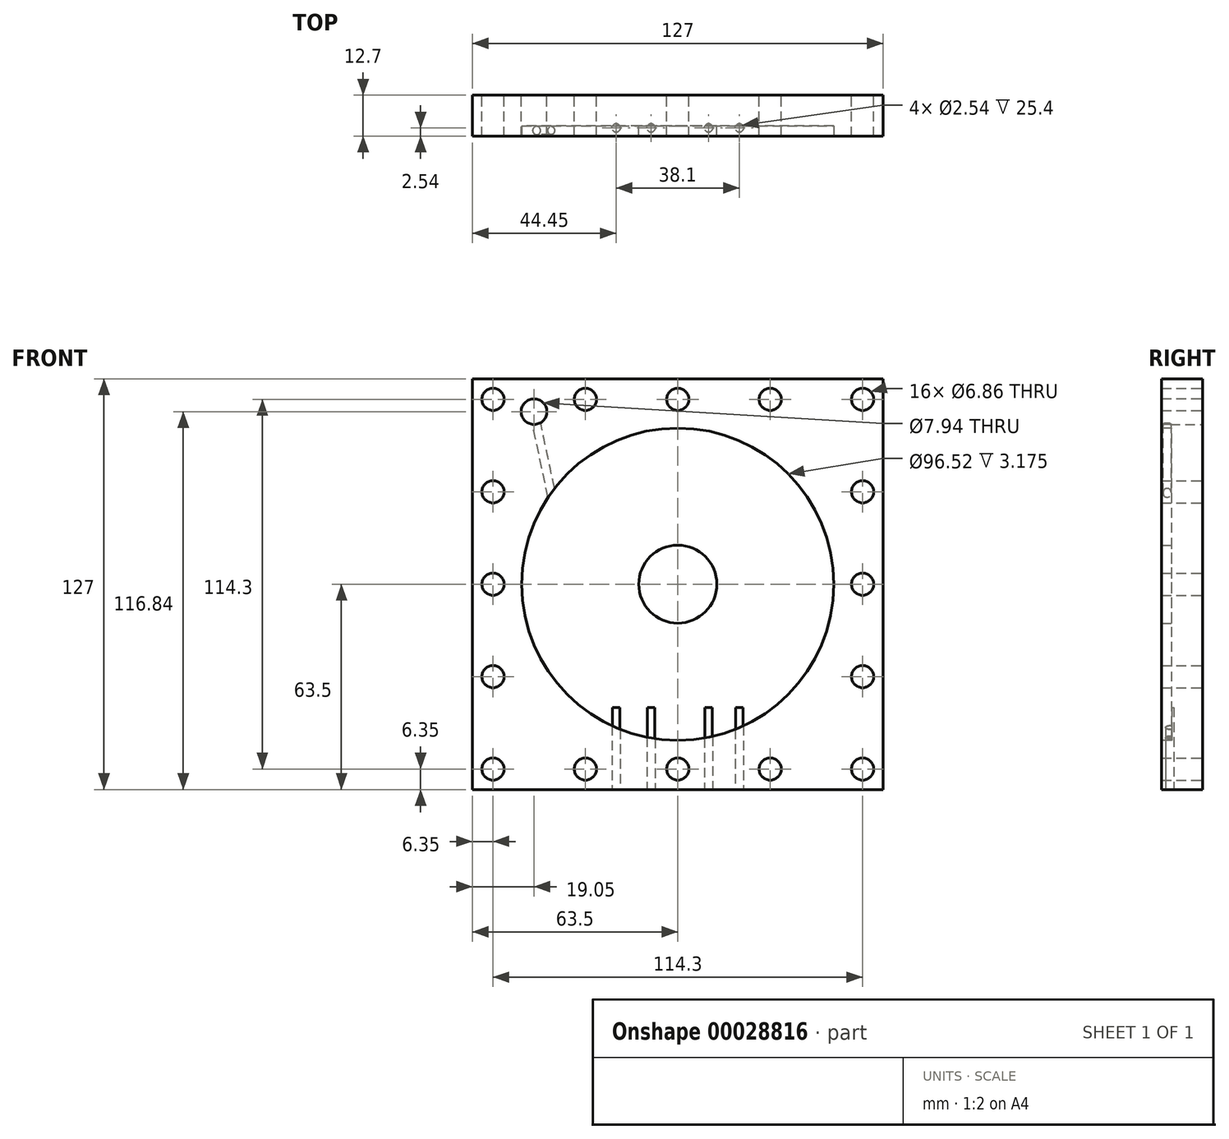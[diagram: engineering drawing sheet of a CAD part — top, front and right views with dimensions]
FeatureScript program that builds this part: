
annotation { "Feature Type Name" : "Feature", "Feature Type Description" : "" }
export const myFeature = defineFeature(function(context is Context, id is Id, definition is map)
    precondition{}
    {
        {
            var Q0;
            Q0=qCreatedBy(makeId("Front.planeOp"),FACE);
            var sketch = newSketch(context, id + "F0", { "sketchPlane" : qUnion([Q0])});
            skLineSegment(sketch, "E0.rect.bottom", {"start": v(63.5, 63.5) * mm, "end": v(-63.5, 63.5) * mm});
            skLineSegment(sketch, "E0.rect.top", {"start": v(63.5, -63.5) * mm, "end": v(-63.5, -63.5) * mm});
            skLineSegment(sketch, "E0.rect.left", {"start": v(63.5, 63.5) * mm, "end": v(63.5, -63.5) * mm});
            skLineSegment(sketch, "E0.rect.right", {"start": v(-63.5, 63.5) * mm, "end": v(-63.5, -63.5) * mm});
            skPoint(sketch, "E0.rect.middle", {"position": v(0, 0) * mm});
            skCircle(sketch, "E1", {"center": v(-44.45, 53.34) * mm, "radius": 3.97 * mm});
            skCircle(sketch, "E2", {"center": v(0, 0) * mm, "radius": 47.56 * mm, "construction": true});
            skLineSegment(sketch, "E3.rect.bottom", {"start": v(-57.15, 57.15) * mm, "end": v(57.15, 57.15) * mm, "construction": true});
            skLineSegment(sketch, "E3.rect.top", {"start": v(-57.15, -57.15) * mm, "end": v(57.15, -57.15) * mm, "construction": true});
            skLineSegment(sketch, "E3.rect.left", {"start": v(-57.15, 57.15) * mm, "end": v(-57.15, -57.15) * mm, "construction": true});
            skLineSegment(sketch, "E3.rect.right", {"start": v(57.15, 57.15) * mm, "end": v(57.15, -57.15) * mm, "construction": true});
            skPoint(sketch, "E4", {"position": v(0, 57.15) * mm});
            skPoint(sketch, "E5", {"position": v(57.15, 0) * mm});
            skPoint(sketch, "E6", {"position": v(0, -57.15) * mm});
            skPoint(sketch, "E7", {"position": v(-57.15, 0) * mm});
            skCircle(sketch, "E8", {"center": v(-57.15, 57.15) * mm, "radius": 3.43 * mm});
            skCircle(sketch, "E9", {"center": v(0, 57.15) * mm, "radius": 3.43 * mm});
            skCircle(sketch, "E10", {"center": v(57.15, 57.15) * mm, "radius": 3.43 * mm});
            skCircle(sketch, "E11", {"center": v(57.15, 0) * mm, "radius": 3.43 * mm});
            skCircle(sketch, "E12", {"center": v(57.15, -57.15) * mm, "radius": 3.43 * mm});
            skCircle(sketch, "E13", {"center": v(0, -57.15) * mm, "radius": 3.43 * mm});
            skCircle(sketch, "E14", {"center": v(-57.15, -57.15) * mm, "radius": 3.43 * mm});
            skCircle(sketch, "E15", {"center": v(-57.15, 0) * mm, "radius": 3.43 * mm});
            skLineSegment(sketch, "E16.rect.bottom", {"start": v(-50, 50) * mm, "end": v(50, 50) * mm, "construction": true});
            skLineSegment(sketch, "E16.rect.top", {"start": v(-50, -50) * mm, "end": v(50, -50) * mm, "construction": true});
            skLineSegment(sketch, "E16.rect.left", {"start": v(-50, 50) * mm, "end": v(-50, -50) * mm, "construction": true});
            skLineSegment(sketch, "E16.rect.right", {"start": v(50, 50) * mm, "end": v(50, -50) * mm, "construction": true});
            skCircle(sketch, "E17", {"center": v(28.57, 57.15) * mm, "radius": 3.43 * mm});
            skCircle(sketch, "E18", {"center": v(57.15, 28.58) * mm, "radius": 3.43 * mm});
            skCircle(sketch, "E19", {"center": v(57.15, -28.58) * mm, "radius": 3.43 * mm});
            skCircle(sketch, "E20", {"center": v(28.58, -57.15) * mm, "radius": 3.43 * mm});
            skCircle(sketch, "E21", {"center": v(-28.58, -57.15) * mm, "radius": 3.43 * mm});
            skCircle(sketch, "E22", {"center": v(-57.15, -28.58) * mm, "radius": 3.43 * mm});
            skCircle(sketch, "E23", {"center": v(-57.15, 28.58) * mm, "radius": 3.43 * mm});
            skCircle(sketch, "E24", {"center": v(-28.58, 57.15) * mm, "radius": 3.43 * mm});
            skSolve(sketch);
        }
        {
            var Q0;
            Q0=qSketchRegion(id+"F0",true);
            var Q1;
            {var subQ21=sQuery(id+"F0.wireOp",EDGE,"f6949425-b88c-4a0e-8302-07c829dae053.0");var subQ27=sQuery(id+"F0.wireOp",EDGE,"5bd9be1d-ee3e-4944-9718-c5885c81100e");var subQ29=makeQuery(id+"F0.imprint","INTERSECT",VERTEX,{"derivedFrom":[subQ21,subQ27]});Q1=makeQuery(id+"F0.imprint","IMPRINT",FACE,{"disambiguationData":[TD([[makeQuery(id+"F0.imprint","IMPRINT",EDGE,{"disambiguationData":[TD([[subQ29,-1.0]])],"derivedFrom":subQ21}),-1.0]])]});}
            extrude(context, id + "F1", {"entities" : qUnion([Q0, Q1]), "depth" : 12.7 * mm});
        }
        {
            var Q0;
            Q0=makeQuery(id+"F1.opExtrude","CAP_FACE",FACE,{"disambiguationData":[OSD([sQuery(id+"F0.wireOp",EDGE,"E0.rect.bottom"),sQuery(id+"F0.wireOp",EDGE,"E0.rect.top"),sQuery(id+"F0.wireOp",EDGE,"E0.rect.left"),sQuery(id+"F0.wireOp",EDGE,"E0.rect.right"),sQuery(id+"F0.wireOp",EDGE,"1b772a9f-1761-4584-9b2b-9508be88e127"),sQuery(id+"F0.wireOp",EDGE,"5bd9be1d-ee3e-4944-9718-c5885c81100e"),sQuery(id+"F0.wireOp",EDGE,"a4b3396b-acb1-4126-9ecc-f22d3d9e1673"),sQuery(id+"F0.wireOp",EDGE,"6f9071d3-dfce-459a-96f3-6cfad81b1998"),sQuery(id+"F0.wireOp",EDGE,"8e253895-448c-4740-8d73-7ad6095a0958"),sQuery(id+"F0.wireOp",EDGE,"49ddc21f-956a-45ed-accb-e36c5fb570fd"),sQuery(id+"F0.wireOp",EDGE,"4c855955-bd80-4a33-8133-648448e085db"),sQuery(id+"F0.wireOp",EDGE,"5388e59b-5754-40e4-abb9-c8fe2573278b"),sQuery(id+"F0.wireOp",EDGE,"cb97a597-6742-4d9a-a243-e93a22987a54"),sQuery(id+"F0.wireOp",EDGE,"2f3ac294-263d-4671-b671-df59b6b99c8d")])],"isStart":false});
            var sketch = newSketch(context, id + "F2", { "sketchPlane" : qUnion([Q0])});
            skCircle(sketch, "E25", {"center": v(0, 0) * mm, "radius": 48.26 * mm});
            skSolve(sketch);
        }
        {
            var Q0;
            Q0=qSketchRegion(id+"F2",true);
            extrude(context, id + "F3", {"entities" : qUnion([Q0]), "operationType" : NewBodyOperationType.REMOVE, "oppositeDirection" : true, "depth" : 3.17 * mm});
        }
        {
            var Q0;
            Q0=makeQuery(id+"F3.boolean.opBoolean","COPY",FACE,{"derivedFrom":makeQuery(id+"F3.opExtrude","CAP_FACE",FACE,{"disambiguationData":[OSD([sQuery(id+"F2.wireOp",EDGE,"E25")])],"isStart":false})});
            var sketch = newSketch(context, id + "F4", { "sketchPlane" : qUnion([Q0])});
            skCircle(sketch, "E26", {"center": v(0, 0) * mm, "radius": 12.07 * mm});
            skSolve(sketch);
        }
        {
            var Q0;
            Q0=qSketchRegion(id+"F4",true);
            extrude(context, id + "F5", {"entities" : qUnion([Q0]), "operationType" : NewBodyOperationType.ADD, "depth" : 3.17 * mm});
        }
        {
            var Q0;
            Q0=makeQuery(id+"F1.opExtrude","CAP_FACE",FACE,{"disambiguationData":[OSD([sQuery(id+"F0.wireOp",EDGE,"E0.rect.bottom"),sQuery(id+"F0.wireOp",EDGE,"E0.rect.top"),sQuery(id+"F0.wireOp",EDGE,"E0.rect.left"),sQuery(id+"F0.wireOp",EDGE,"E0.rect.right"),sQuery(id+"F0.wireOp",EDGE,"E1"),sQuery(id+"F0.wireOp",EDGE,"E8"),sQuery(id+"F0.wireOp",EDGE,"E9"),sQuery(id+"F0.wireOp",EDGE,"E10"),sQuery(id+"F0.wireOp",EDGE,"E11"),sQuery(id+"F0.wireOp",EDGE,"E12"),sQuery(id+"F0.wireOp",EDGE,"E13"),sQuery(id+"F0.wireOp",EDGE,"E14"),sQuery(id+"F0.wireOp",EDGE,"E15")])],"isStart":false});
            var sketch = newSketch(context, id + "F6", { "sketchPlane" : qUnion([Q0])});
            skLineSegment(sketch, "E27", {"start": v(-44.45, 53.34) * mm, "end": v(-94.91, 42.61) * mm, "construction": true});
            skSolve(sketch);
        }
        {
            var Q0;
            Q0=sQuery(id+"F6.wireOp",EDGE,"E27");
            cPlane(context, id + "F7", {"entities" : qUnion([Q0]), "cplaneType" : CPlaneType.LINE_ANGLE, "offset" : 152.4 * mm, "angle" : 90 * degree, "width" : 152.4 * mm, "height" : 152.4 * mm});
        }
        {
            var Q0;
            Q0=qCreatedBy(id+"F7.planeOp",FACE);
            var sketch = newSketch(context, id + "F8", { "sketchPlane" : qUnion([Q0])});
            skCircle(sketch, "E28", {"center": v(-32.39, -10.95) * mm, "radius": 1.27 * mm});
            skLineSegment(sketch, "E29", {"start": v(-32.39, -10.95) * mm, "end": v(-32.39, -12.7) * mm, "construction": true});
            skSolve(sketch);
        }
        {
            var Q0;
            Q0=qSketchRegion(id+"F8",true);
            var Q1;
            Q1=makeQuery(id+"F3.boolean.opBoolean","COPY",FACE,{"derivedFrom":makeQuery(id+"F3.opExtrude","SWEPT_FACE",FACE,{"disambiguationData":[OSD([sQuery(id+"F2.wireOp",EDGE,"E25")])]})});
            extrude(context, id + "F9", {"entities" : qUnion([Q0]), "operationType" : NewBodyOperationType.REMOVE, "endBound" : BoundingType.UP_TO_SURFACE, "oppositeDirection" : true, "endBoundEntityFace" : qUnion([Q1]), "depth" : 25.4 * mm});
        }
        {
            var Q0;
            Q0=makeQuery(id+"F1.opExtrude","SWEPT_FACE",FACE,{"disambiguationData":[OSD([sQuery(id+"F0.wireOp",EDGE,"E0.rect.top")])]});
            var sketch = newSketch(context, id + "F10", { "sketchPlane" : qUnion([Q0])});
            skCircle(sketch, "E30", {"center": v(-19.05, 10.16) * mm, "radius": 1.27 * mm});
            skCircle(sketch, "E31", {"center": v(-8.25, 10.16) * mm, "radius": 1.27 * mm});
            skCircle(sketch, "E32", {"center": v(9.53, 10.16) * mm, "radius": 1.27 * mm});
            skCircle(sketch, "E33", {"center": v(19.05, 10.16) * mm, "radius": 1.27 * mm});
            skSolve(sketch);
        }
        {
            var Q0;
            Q0 = qSketchRegion(id + "F10", true);
            extrude(context, id + "F11", {"entities" : qUnion([Q0]), "operationType" : NewBodyOperationType.REMOVE, "oppositeDirection" : true, "depth" : 25.4 * mm});
        }
    });
